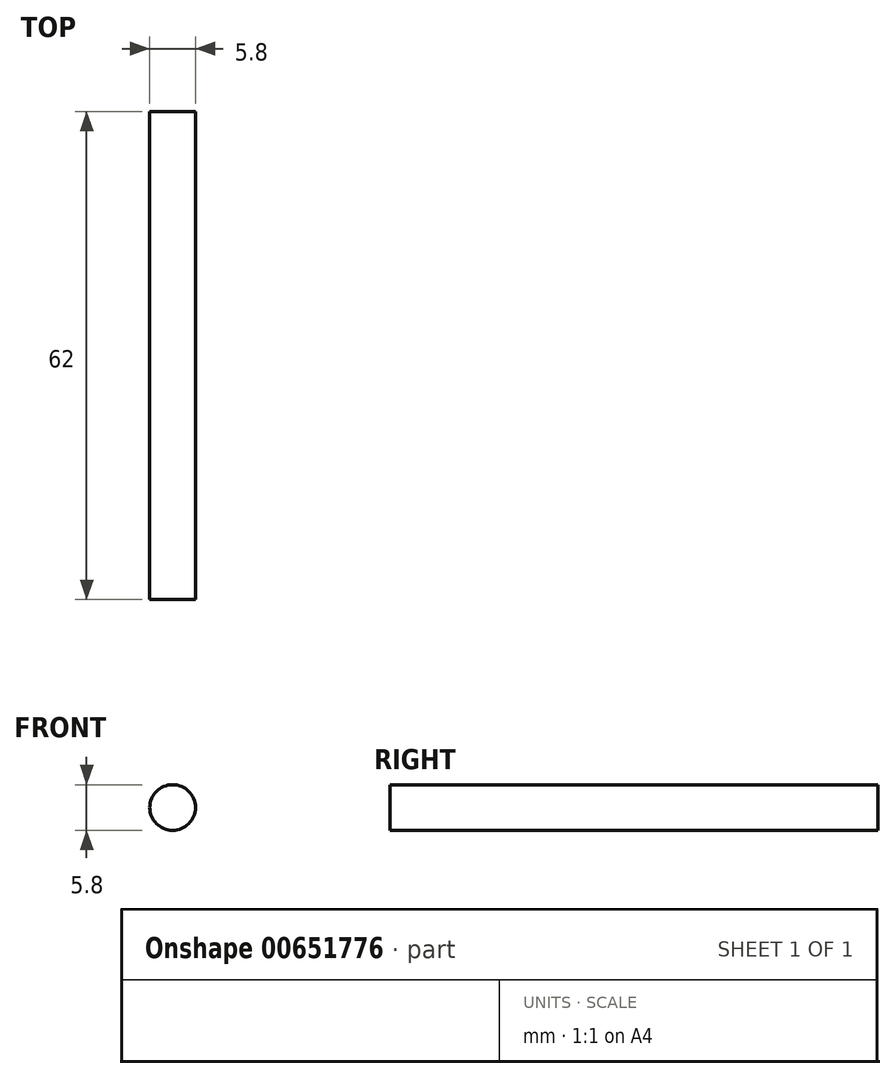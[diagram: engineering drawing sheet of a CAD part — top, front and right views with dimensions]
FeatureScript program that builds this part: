
annotation { "Feature Type Name" : "Feature", "Feature Type Description" : "" }
export const myFeature = defineFeature(function(context is Context, id is Id, definition is map)
    precondition{}
    {
        {
            var Q0;
            Q0=qCreatedBy(makeId("Front.planeOp"),FACE);
            var sketch = newSketch(context, id + "F0", { "sketchPlane" : qUnion([Q0])});
            skCircle(sketch, "E0", {"center": v(0, -3.3) * mm, "radius": 2.9 * mm});
            skSolve(sketch);
        }
        {
            var Q0;
            Q0=makeQuery(id+"F0.imprint","IMPRINT",FACE,{"disambiguationData":[TD([[makeQuery(id+"F0.imprint","IMPRINT",EDGE,{"derivedFrom":sQuery(id+"F0.wireOp",EDGE,"E0")}),1.0]])]});
            extrude(context, id + "F1", {"entities" : qUnion([Q0]), "endBound" : BoundingType.SYMMETRIC, "depth" : 62 * mm, "offsetDistance" : 25 * mm});
        }
    });
